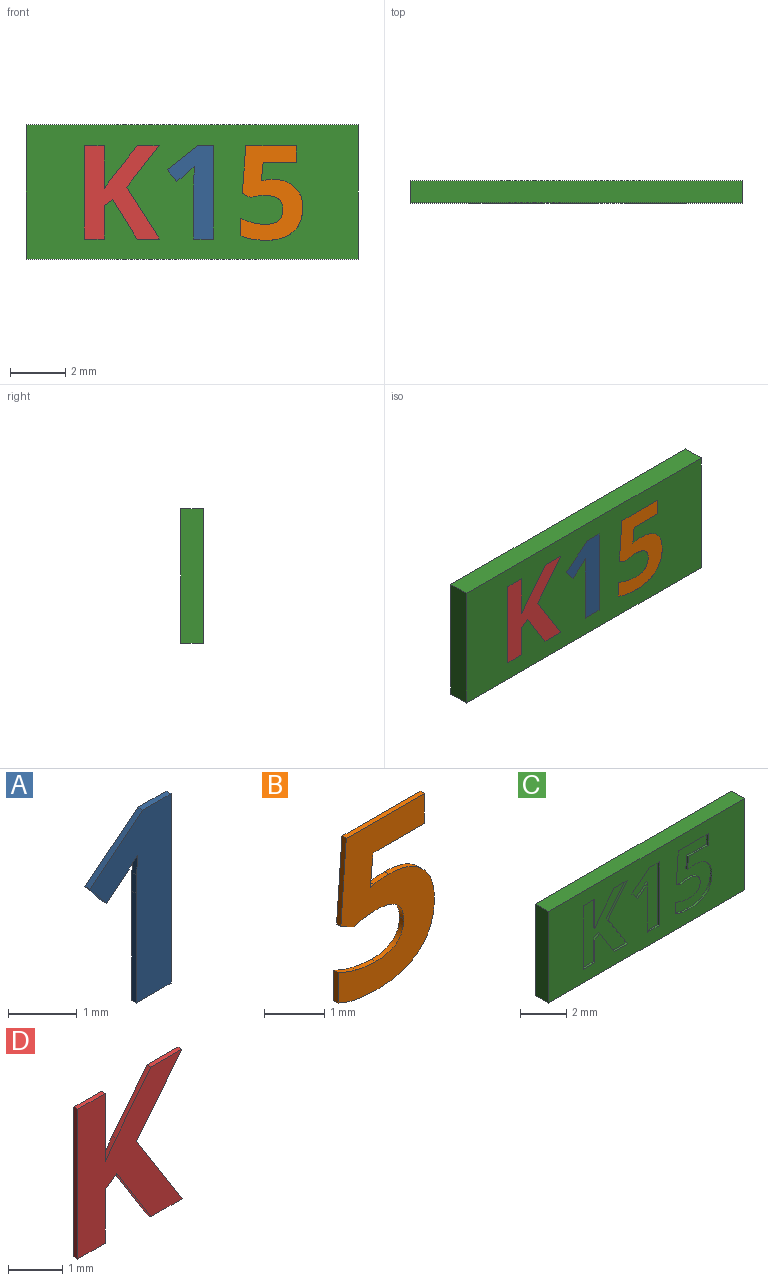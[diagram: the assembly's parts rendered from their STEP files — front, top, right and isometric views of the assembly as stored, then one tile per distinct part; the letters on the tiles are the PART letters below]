
ASSEMBLY  parts=4 mates=3
PART A: 12 faces, bbox 1.7x0.1x3.4 mm
  f0: plane 3.37x1.67mm, normal (0,-1,0), area 2.9mm2, adj f1,f2,f3,f4,f5,f6,f7,f9
  f1: plane 0.59x0.1mm, normal (0,0,1), area 0.1mm2, adj f0,f2,f8,f10
  f2: plane 1.09x0.86mm, normal (-0.62,0,0.78), area 0.1mm2, adj f0,f1,f3,f8
  f3: plane 0.43x0.34mm, normal (-0.78,0,-0.63), area 0.1mm2, adj f0,f2,f4,f8
  f4: plane 0.39x0.31mm, normal (0.63,0,-0.78), area 0mm2, adj f0,f3,f5,f8
  f5: extruded ~0.25x0.23mm, area 0mm2, adj f0,f4,f6,f8
  f6: plane 0.35x0.1mm, normal (-1,0,0.03), area 0mm2, adj f0,f5,f7,f8
  f7: plane 0.32x0.1mm, normal (-1,0,0.02), area 0mm2, adj f0,f6,f8,f9
  f8: plane 3.37x1.67mm, normal (0,1,0), area 2.9mm2, adj f1,f2,f3,f4,f5,f6,f7,f9
  f9: plane 1.95x0.1mm, normal (-1,0,0), area 0.2mm2, adj f0,f7,f8,f11
  f10: plane 3.37x0.1mm, normal (1,0,0), area 0.3mm2, adj f0,f1,f8,f11
  f11: plane 0.71x0.1mm, normal (0,0,-1), area 0.1mm2, adj f0,f8,f9,f10
PART B: 22 faces, bbox 2.3x0.1x3.4 mm
  f0: plane 3.42x2.25mm, normal (0,-1,0), area 4.5mm2, adj f1,f2,f3,f4,f5,f6,f7,f8
  f1: plane 0.1x0.08mm, normal (-0.2,0,0.98), area 0mm2, adj f0,f2,f18,f20
  f2: plane 0.66x0.1mm, normal (1,0,-0.09), area 0.1mm2, adj f0,f1,f3,f18
  f3: plane 1.2x0.1mm, normal (0,0,-1), area 0.1mm2, adj f0,f2,f4,f18
  f4: plane 0.6x0.1mm, normal (1,0,0), area 0.1mm2, adj f0,f3,f5,f18
  f5: plane 1.83x0.1mm, normal (0,0,1), area 0.2mm2, adj f0,f4,f6,f18
  f6: plane 1.72x0.13mm, normal (-1,0,0.07), area 0.2mm2, adj f0,f5,f7,f18
  f7: plane 0.28x0.15mm, normal (-0.47,0,-0.88), area 0mm2, adj f0,f6,f8,f18
  f8: extruded ~0.24x0.1mm, area 0mm2, adj f0,f7,f9,f18
  f9: extruded ~0.27x0.1mm, area 0mm2, adj f0,f8,f10,f18
  f10: extruded ~0.68x0.51mm, area 0.1mm2, adj f0,f9,f11,f18
  f11: extruded ~0.65x0.54mm, area 0.1mm2, adj f0,f10,f12,f18
  f12: extruded ~0.46x0.1mm, area 0mm2, adj f0,f11,f13,f18
  f13: extruded ~0.42x0.16mm, area 0mm2, adj f0,f12,f14,f18
  f14: plane 0.62x0.1mm, normal (-1,0,0), area 0.1mm2, adj f0,f13,f15,f18
  f15: extruded ~0.91x0.18mm, area 0.1mm2, adj f0,f14,f16,f18
  f16: extruded ~1x0.3mm, area 0.1mm2, adj f0,f15,f17,f18
  f17: extruded ~0.87x0.35mm, area 0.1mm2, adj f0,f16,f18,f19
  f18: plane 3.42x2.25mm, normal (0,1,0), area 4.5mm2, adj f1,f2,f3,f4,f5,f6,f7,f8
  f19: extruded ~0.75x0.29mm, area 0.1mm2, adj f0,f17,f18,f21
  f20: extruded ~0.35x0.1mm, area 0mm2, adj f0,f1,f18,f21
  f21: extruded ~0.78x0.27mm, area 0.1mm2, adj f0,f18,f19,f20
PART C: 52 faces, bbox 12x0.8x4.9 mm
  f0: plane 12x4.85mm, normal (0,-1,0), area 45.6mm2, adj f1,f2,f3,f4,f6,f7,f8,f9
  f1: plane 12x0.8mm, normal (0,0,-1), area 9.6mm2, adj f0,f2,f4,f5
  f2: plane 4.85x0.8mm, normal (1,0,0), area 3.9mm2, adj f0,f1,f3,f5
  f3: plane 12x0.8mm, normal (0,0,1), area 9.6mm2, adj f0,f2,f4,f5
  f4: plane 4.85x0.8mm, normal (-1,0,0), area 3.9mm2, adj f0,f1,f3,f5
  f5: plane 12x4.85mm, normal (0,1,0), area 58.2mm2, adj f1,f2,f3,f4
  f6: extruded ~0.35x0.1mm, area 0mm2, adj f0,f7,f25,f26
  f7: plane 0.1x0.08mm, normal (0.2,0,-0.98), area 0mm2, adj f0,f6,f8,f26
  f8: plane 0.66x0.1mm, normal (-1,0,0.09), area 0.1mm2, adj f0,f7,f9,f26
  f9: plane 1.2x0.1mm, normal (0,0,1), area 0.1mm2, adj f0,f8,f10,f26
  f10: plane 0.6x0.1mm, normal (-1,0,0), area 0.1mm2, adj f0,f9,f11,f26
  f11: plane 1.83x0.1mm, normal (0,0,-1), area 0.2mm2, adj f0,f10,f12,f26
  f12: plane 1.72x0.13mm, normal (1,0,-0.07), area 0.2mm2, adj f0,f11,f13,f26
  f13: plane 0.28x0.15mm, normal (0.47,0,0.88), area 0mm2, adj f0,f12,f14,f26
  f14: extruded ~0.24x0.1mm, area 0mm2, adj f0,f13,f15,f26
  f15: extruded ~0.27x0.1mm, area 0mm2, adj f0,f14,f16,f26
  f16: extruded ~0.68x0.51mm, area 0.1mm2, adj f0,f15,f17,f26
  f17: extruded ~0.65x0.54mm, area 0.1mm2, adj f0,f16,f18,f26
  f18: extruded ~0.46x0.1mm, area 0mm2, adj f0,f17,f19,f26
  f19: extruded ~0.42x0.16mm, area 0mm2, adj f0,f18,f20,f26
  f20: plane 0.62x0.1mm, normal (1,0,0), area 0.1mm2, adj f0,f19,f21,f26
  f21: extruded ~0.91x0.18mm, area 0.1mm2, adj f0,f20,f22,f26
  f22: extruded ~1x0.3mm, area 0.1mm2, adj f0,f21,f23,f26
  f23: extruded ~0.87x0.35mm, area 0.1mm2, adj f0,f22,f24,f26
  f24: extruded ~0.75x0.29mm, area 0.1mm2, adj f0,f23,f25,f26
  f25: extruded ~0.78x0.27mm, area 0.1mm2, adj f0,f6,f24,f26
  f26: plane 3.42x2.25mm, normal (0,-1,0), area 4.5mm2, adj f6,f7,f8,f9,f10,f11,f12,f13
  f27: plane 3.37x0.1mm, normal (-1,0,0), area 0.3mm2, adj f0,f28,f36,f37
  f28: plane 0.59x0.1mm, normal (0,0,-1), area 0.1mm2, adj f0,f27,f29,f37
  f29: plane 1.09x0.86mm, normal (0.62,0,-0.78), area 0.1mm2, adj f0,f28,f30,f37
  f30: plane 0.43x0.34mm, normal (0.78,0,0.63), area 0.1mm2, adj f0,f29,f31,f37
  f31: plane 0.39x0.31mm, normal (-0.63,0,0.78), area 0mm2, adj f0,f30,f32,f37
  f32: extruded ~0.25x0.23mm, area 0mm2, adj f0,f31,f33,f37
  f33: plane 0.35x0.1mm, normal (1,0,-0.03), area 0mm2, adj f0,f32,f34,f37
  f34: plane 0.32x0.1mm, normal (1,0,-0.02), area 0mm2, adj f0,f33,f35,f37
  f35: plane 1.95x0.1mm, normal (1,0,0), area 0.2mm2, adj f0,f34,f36,f37
  f36: plane 0.71x0.1mm, normal (0,0,1), area 0.1mm2, adj f0,f27,f35,f37
  f37: plane 3.37x1.67mm, normal (0,-1,0), area 2.9mm2, adj f27,f28,f29,f30,f31,f32,f33,f34
  f38: plane 1.88x1.19mm, normal (-0.85,0,-0.53), area 0.2mm2, adj f0,f39,f50,f51
  f39: plane 1.49x1.18mm, normal (-0.79,0,0.62), area 0.2mm2, adj f0,f38,f40,f51
  f40: plane 0.79x0.1mm, normal (0,0,-1), area 0.1mm2, adj f0,f39,f41,f51
  f41: plane 1.15x0.91mm, normal (0.78,0,-0.62), area 0.1mm2, adj f0,f40,f42,f51
  f42: plane 0.4x0.28mm, normal (0.82,0,-0.58), area 0mm2, adj f0,f41,f43,f51
  f43: plane 1.54x0.1mm, normal (-1,0,0), area 0.2mm2, adj f0,f42,f44,f51
  f44: plane 0.72x0.1mm, normal (0,0,-1), area 0.1mm2, adj f0,f43,f45,f51
  f45: plane 3.37x0.1mm, normal (1,0,0), area 0.3mm2, adj f0,f44,f46,f51
  f46: plane 0.72x0.1mm, normal (0,0,1), area 0.1mm2, adj f0,f45,f47,f51
  f47: plane 1.2x0.1mm, normal (-1,0,0), area 0.1mm2, adj f0,f46,f48,f51
  f48: plane 0.3x0.22mm, normal (-0.58,0,0.81), area 0mm2, adj f0,f47,f49,f51
  f49: plane 1.42x0.88mm, normal (0.85,0,0.53), area 0.2mm2, adj f0,f48,f50,f51
  f50: plane 0.81x0.1mm, normal (0,0,1), area 0.1mm2, adj f0,f38,f49,f51
  f51: plane 3.37x2.71mm, normal (0,-1,0), area 5.2mm2, adj f38,f39,f40,f41,f42,f43,f44,f45
PART D: 15 faces, bbox 2.7x0.1x3.4 mm
  f0: plane 3.37x2.71mm, normal (0,-1,0), area 5.2mm2, adj f1,f2,f3,f4,f5,f6,f7,f8
  f1: plane 1.49x1.18mm, normal (0.79,0,-0.62), area 0.2mm2, adj f0,f2,f11,f13
  f2: plane 0.79x0.1mm, normal (0,0,1), area 0.1mm2, adj f0,f1,f3,f11
  f3: plane 1.15x0.91mm, normal (-0.78,0,0.62), area 0.1mm2, adj f0,f2,f4,f11
  f4: plane 0.4x0.28mm, normal (-0.82,0,0.58), area 0mm2, adj f0,f3,f5,f11
  f5: plane 1.54x0.1mm, normal (1,0,0), area 0.2mm2, adj f0,f4,f6,f11
  f6: plane 0.72x0.1mm, normal (0,0,1), area 0.1mm2, adj f0,f5,f7,f11
  f7: plane 3.37x0.1mm, normal (-1,0,0), area 0.3mm2, adj f0,f6,f8,f11
  f8: plane 0.72x0.1mm, normal (0,0,-1), area 0.1mm2, adj f0,f7,f9,f11
  f9: plane 1.2x0.1mm, normal (1,0,0), area 0.1mm2, adj f0,f8,f10,f11
  f10: plane 0.3x0.22mm, normal (0.58,0,-0.81), area 0mm2, adj f0,f9,f11,f12
  f11: plane 3.37x2.71mm, normal (0,1,0), area 5.2mm2, adj f1,f2,f3,f4,f5,f6,f7,f8
  f12: plane 1.42x0.88mm, normal (-0.85,0,-0.53), area 0.2mm2, adj f0,f10,f11,f14
  f13: plane 1.88x1.19mm, normal (0.85,0,0.53), area 0.2mm2, adj f0,f1,f11,f14
  f14: plane 0.81x0.1mm, normal (0,0,-1), area 0.1mm2, adj f0,f11,f12,f13
PLACE A t=(-1.64,0.4,-0.03)mm
PLACE B t=(1.32,0.4,-0.03)mm
PLACE C t=(-0.03,0.4,-0.03)mm
PLACE D t=(-1.64,0.4,-0.03)mm
MATE fastened A.f0 <-> C.f0  axis (0,-1,0) through (0.03,-0.4,-1.73)mm
MATE fastened B.f0 <-> C.f0  axis (0,-1,0) through (1.72,-0.4,-1.6)mm
MATE fastened D.f0 <-> C.f0  axis (0,-1,0) through (-3.92,-0.4,-1.73)mm
